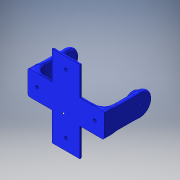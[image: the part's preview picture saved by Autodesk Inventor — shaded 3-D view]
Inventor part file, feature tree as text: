
AUTODESK INVENTOR PART (.ipt)
format: ipt  version: 2016 (Build 200138000, 138)  size: 476,672 bytes
history: native  units: in
note: dims shown in document units (in); Inventor stores cm internally (conversion verified against a paired STEP export)
features: sketch x11, fillet x10, extrude x9, hole x2
ambient origin geometry x8: Origin, YZ Plane, XZ Plane, XY Plane, X Axis, Y Axis, Z Axis, Center Point
bodies: Solid1 (feature_tree)
feature tree (32):
  extrude  "Extrusion1"  Depth=0.5197in
  extrude  "Extrusion3"  Depth=0.0787in
  sketch  "Sketch5"  dims[d9=0.9449in d10=0.0in d11=0.2835in]
  extrude  "Extrusion4"  Depth=0.2835in
  extrude  "Extrusion5"  Depth=0.2598in
  fillet  "Fillet1"  Radius=0.2598in
  fillet  "Fillet4"  Radius=0.5197in
  fillet  "Fillet5"  Radius=0.3622in
  fillet  "Fillet6"  Radius=0.1437in
  fillet  "Fillet7"  Radius=0.5551in
  extrude  "Extrusion6"  Depth=0.0787in TaperAngle=0.0deg
  fillet  "Fillet8"  Radius=0.0787in
  sketch  "Sketch9"  dims[d19=0.2224in d24=0.0787in d25=0.0in d26=0.0787in]
  extrude  "Extrusion7"  Depth=0.0787in TaperAngle=0.0deg
  fillet  "Fillet10"  Radius=0.1969in
  fillet  "Fillet11"  Radius=0.0394in
  sketch  "Sketch10"  dims[d27=0.0787in d28=0.0787in d29=0.0in d30=0.1969in d33=0.0394in]
  extrude  "Extrusion8"  Depth=0.0394in
  extrude  "Extrusion10"  Depth=0.0197in
  extrude  "Extrusion11"  Depth=0.1969in
  hole  "Hole2"  [1 undecoded]
  fillet  "Fillet15"  Radius=0.2598in
  fillet  "Fillet16"  Radius=0.1181in
  sketch  "Sketch18"  dims[d43=0.2598in d44=0.2598in d45=0.2598in d46=0.1181in]
  hole  "Hole3"  [1 undecoded]
  sketch  "Sketch1"  dims[d0=1.6142in d1=0.5197in]
  sketch  "Sketch4"  dims[d2=0.0787in d3=0.0in d8=0.0787in]
  sketch  "Sketch7"  dims[d12=0.2598in d13=0.2598in d14=0.2598in d15=0.5197in d16=0.3622in d17=0.1437in d18=0.5551in]
  sketch  "Sketch15"  dims[d34=0.0394in d35=0.0394in]
  sketch  "Sketch16"  dims[d36=0.0197in d37=0.0787in]
  sketch  "Sketch17"  dims[d38=0.9449in d39=0.0in d40=0.1969in]
  sketch  "Sketch19"  dims[d47=0.1181in d48=0.0in d49=0.0394in d50=0.0394in d51=0.1181in d52=0.1181in d53=0.0in d79=0.5118in d80=0.5118in d81=0.6043in d82=0.0in d83=0.5118in d84=0.5118in d85=0.6043in d86=0.0in d87=0.2953in d88=0.2953in d89=0.2598in d90=0.2598in d91=0.1969in d92=0.2362in d93=0.2953in d94=0.2953in d95=0.2362in d96=0.2598in d97=0.2598in d98=0.1969in d99=0.0591in d100=0.2362in d101=0.1575in d102=0.0787in d103=90.0deg d104=0.1181in d105=0.8108in d106=0.0748in d107=0.0354in d108=0.0394in d109=0.2362in d110=0.1575in d111=0.0787in d112=90.0deg d113=0.315in d114=0.8108in]
note: 2 required parameter values undecoded (feature->parameter linkage not recoverable at this tier; creation-order binding heuristic only, values carry confidence <= 0.55)
